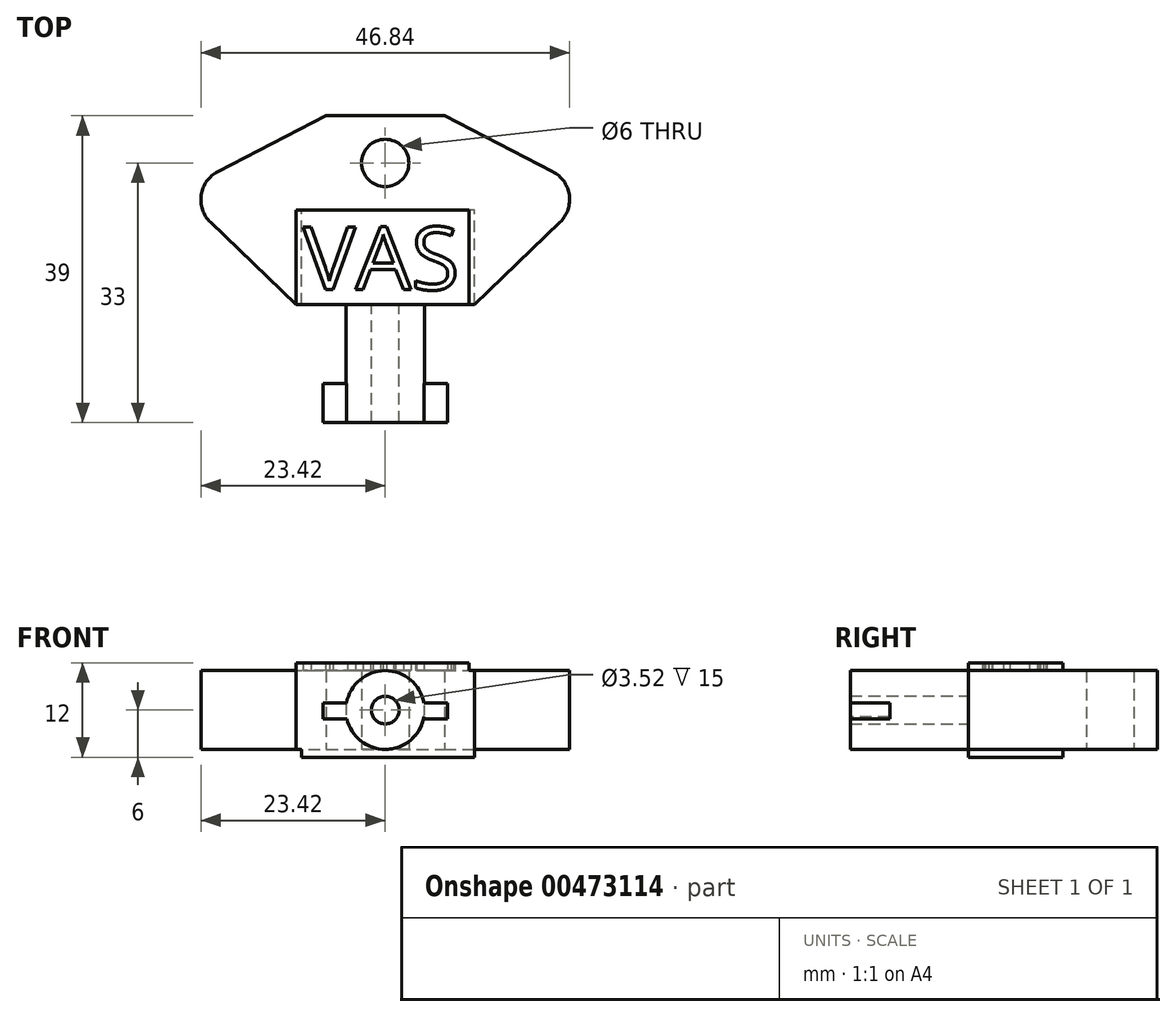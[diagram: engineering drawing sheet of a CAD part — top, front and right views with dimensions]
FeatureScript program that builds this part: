
annotation { "Feature Type Name" : "Feature", "Feature Type Description" : "" }
export const myFeature = defineFeature(function(context is Context, id is Id, definition is map)
    precondition{}
    {
        {
            var Q0;
            Q0=qCreatedBy(makeId("Top.planeOp"),FACE);
            var sketch = newSketch(context, id + "F0", { "sketchPlane" : qUnion([Q0])});
            skCircle(sketch, "E0", {"center": v(0, 0) * mm, "radius": 3 * mm});
            skLineSegment(sketch, "E1", {"start": v(-7.5, 6) * mm, "end": v(7.5, 6) * mm});
            skLineSegment(sketch, "E2", {"start": v(7.5, 6) * mm, "end": v(21.25, -1.1) * mm});
            skLineSegment(sketch, "E3", {"start": v(22.2, -7.53) * mm, "end": v(11.35, -18) * mm});
            skLineSegment(sketch, "E4", {"start": v(-11.35, -18) * mm, "end": v(-22.2, -7.53) * mm});
            skLineSegment(sketch, "E5", {"start": v(-21.25, -1.1) * mm, "end": v(-7.5, 6) * mm});
            skPoint(sketch, "E6", {"position": v(0, -18) * mm});
            skPoint(sketch, "E7", {"position": v(0, 6) * mm});
            skPoint(sketch, "E8.visualSharp", {"position": v(-26.21, -3.66) * mm});
            skArc(sketch, "E8.filletArc", {"start": v(-21.25, -1.1) * mm, "mid": v(-23.38, -4.07) * mm, "end": v(-22.2, -7.53) * mm});
            skPoint(sketch, "E9.visualSharp", {"position": v(26.21, -3.66) * mm});
            skArc(sketch, "E9.filletArc", {"start": v(22.2, -7.53) * mm, "mid": v(23.38, -4.07) * mm, "end": v(21.25, -1.1) * mm});
            skLineSegment(sketch, "E10", {"start": v(11.35, -18) * mm, "end": v(5, -18) * mm});
            skLineSegment(sketch, "E11", {"start": v(-5, -18) * mm, "end": v(-11.35, -18) * mm});
            skLineSegment(sketch, "E12", {"start": v(-5, -18) * mm, "end": v(5, -18) * mm});
            skSolve(sketch);
        }
        {
            var Q0;
            Q0=makeQuery(id+"F0.imprint","IMPRINT",FACE,{"disambiguationData":[TD([[makeQuery(id+"F0.imprint","IMPRINT",EDGE,{"derivedFrom":sQuery(id+"F0.wireOp",EDGE,"E0")}),-1.0]])]});
            extrude(context, id + "F1", {"entities" : qUnion([Q0]), "endBound" : BoundingType.SYMMETRIC, "depth" : 10 * mm});
        }
        {
            var Q0;
            Q0=makeQuery(id+"F1.opExtrude","SWEPT_FACE",FACE,{"disambiguationData":[OSD([sQuery(id+"F0.wireOp",EDGE,"E10"),sQuery(id+"F0.wireOp",EDGE,"E11"),sQuery(id+"F0.wireOp",EDGE,"E12")])]});
            var sketch = newSketch(context, id + "F2", { "sketchPlane" : qUnion([Q0])});
            skCircle(sketch, "E13", {"center": v(0, 0) * mm, "radius": 5 * mm});
            skCircle(sketch, "E14", {"center": v(0, 0) * mm, "radius": 1.76 * mm});
            skSolve(sketch);
        }
        {
            var Q0;
            Q0=makeQuery(id+"F2.imprint","IMPRINT",FACE,{"disambiguationData":[TD([[makeQuery(id+"F2.imprint","IMPRINT",EDGE,{"derivedFrom":sQuery(id+"F2.wireOp",EDGE,"E14")}),-1.0]])]});
            extrude(context, id + "F3", {"entities" : qUnion([Q0]), "operationType" : NewBodyOperationType.ADD, "depth" : 15 * mm});
        }
        {
            var Q0;
            Q0=makeQuery(id+"F3.opExtrude","CAP_FACE",FACE,{"disambiguationData":[OSD([sQuery(id+"F2.wireOp",EDGE,"E13"),sQuery(id+"F2.wireOp",EDGE,"E14")])],"isStart":false});
            var sketch = newSketch(context, id + "F4", { "sketchPlane" : qUnion([Q0])});
            skLineSegment(sketch, "E15.bottom", {"start": v(-4.88, -1.11) * mm, "end": v(-7.88, -1.11) * mm});
            skLineSegment(sketch, "E15.top", {"start": v(-4.88, 0.89) * mm, "end": v(-7.88, 0.89) * mm});
            skLineSegment(sketch, "E15.left", {"start": v(-4.88, -1.11) * mm, "end": v(-4.88, 0.89) * mm});
            skLineSegment(sketch, "E15.right", {"start": v(-7.88, -1.11) * mm, "end": v(-7.88, 0.89) * mm});
            skPoint(sketch, "E16.firstSnap0", {"position": v(-6.38, 0.89) * mm});
            skLineSegment(sketch, "E16.bottom", {"start": v(4.92, 0.89) * mm, "end": v(7.92, 0.89) * mm});
            skLineSegment(sketch, "E16.top", {"start": v(4.92, -1.11) * mm, "end": v(7.92, -1.11) * mm});
            skLineSegment(sketch, "E16.left", {"start": v(4.92, 0.89) * mm, "end": v(4.92, -1.11) * mm});
            skLineSegment(sketch, "E16.right", {"start": v(7.92, 0.89) * mm, "end": v(7.92, -1.11) * mm});
            skSolve(sketch);
        }
        {
            var Q0;
            {var subQ0=sQuery(id+"F4.wireOp",EDGE,"E15.bottom");Q0=makeQuery(id+"F4.imprint","IMPRINT",FACE,{"disambiguationData":[TD([[makeQuery(id+"F4.imprint","IMPRINT",EDGE,{"derivedFrom":subQ0}),-1.0]])]});}
            var Q1;
            {var subQ4=sQuery(id+"F4.wireOp",EDGE,"E16.bottom");Q1=makeQuery(id+"F4.imprint","IMPRINT",FACE,{"disambiguationData":[TD([[makeQuery(id+"F4.imprint","IMPRINT",EDGE,{"derivedFrom":subQ4}),-1.0]])]});}
            extrude(context, id + "F5", {"entities" : qUnion([Q0, Q1]), "operationType" : NewBodyOperationType.ADD, "oppositeDirection" : true, "depth" : 5 * mm});
        }
        {
            var Q0;
            Q0=makeQuery(id+"F1.opExtrude","CAP_FACE",FACE,{"disambiguationData":[OSD([sQuery(id+"F0.wireOp",EDGE,"E0"),sQuery(id+"F0.wireOp",EDGE,"E1"),sQuery(id+"F0.wireOp",EDGE,"E2"),sQuery(id+"F0.wireOp",EDGE,"E3"),sQuery(id+"F0.wireOp",EDGE,"E4"),sQuery(id+"F0.wireOp",EDGE,"E5"),sQuery(id+"F0.wireOp",EDGE,"E8.filletArc"),sQuery(id+"F0.wireOp",EDGE,"E9.filletArc"),sQuery(id+"F0.wireOp",EDGE,"E10"),sQuery(id+"F0.wireOp",EDGE,"E11"),sQuery(id+"F0.wireOp",EDGE,"E12")])],"isStart":true});
            var sketch = newSketch(context, id + "F6", { "sketchPlane" : qUnion([Q0])});
            skLineSegment(sketch, "E17.bottom", {"start": v(11.35, 18) * mm, "end": v(-10.65, 18) * mm});
            skLineSegment(sketch, "E17.top", {"start": v(11.35, 6) * mm, "end": v(-10.65, 6) * mm});
            skLineSegment(sketch, "E17.left", {"start": v(11.35, 18) * mm, "end": v(11.35, 6) * mm});
            skLineSegment(sketch, "E17.right", {"start": v(-10.65, 18) * mm, "end": v(-10.65, 6) * mm});
            skSolve(sketch);
        }
        {
            var Q0;
            Q0 = qSketchRegion(id + "F6", true);
            extrude(context, id + "F7", {"entities" : qUnion([Q0]), "operationType" : NewBodyOperationType.ADD, "depth" : 1 * mm});
        }
        {
            var Q0;
            Q0=makeQuery(id+"F1.opExtrude","CAP_FACE",FACE,{"disambiguationData":[OSD([sQuery(id+"F0.wireOp",EDGE,"E0"),sQuery(id+"F0.wireOp",EDGE,"E1"),sQuery(id+"F0.wireOp",EDGE,"E2"),sQuery(id+"F0.wireOp",EDGE,"E3"),sQuery(id+"F0.wireOp",EDGE,"E4"),sQuery(id+"F0.wireOp",EDGE,"E5"),sQuery(id+"F0.wireOp",EDGE,"E8.filletArc"),sQuery(id+"F0.wireOp",EDGE,"E9.filletArc"),sQuery(id+"F0.wireOp",EDGE,"E10"),sQuery(id+"F0.wireOp",EDGE,"E11"),sQuery(id+"F0.wireOp",EDGE,"E12")])],"isStart":false});
            var sketch = newSketch(context, id + "F8", { "sketchPlane" : qUnion([Q0])});
            skLineSegment(sketch, "E18.bottom", {"start": v(-11.35, -18) * mm, "end": v(10.65, -18) * mm});
            skLineSegment(sketch, "E18.top", {"start": v(-11.35, -6) * mm, "end": v(10.65, -6) * mm});
            skLineSegment(sketch, "E18.left", {"start": v(-11.35, -18) * mm, "end": v(-11.35, -6) * mm});
            skLineSegment(sketch, "E18.right", {"start": v(10.65, -18) * mm, "end": v(10.65, -6) * mm});
            skText(sketch, "E19", { "text": "VAS", "fontName": "OpenSans-Regular.ttf"});
            const initialGuessF8  = {"E19": [-0.01041, -0.0161, 1, 0, 0.00803]};
            skSetInitialGuess(sketch, initialGuessF8);
            skSolve(sketch);
        }
        {
            var Q0;
            Q0=makeQuery(id+"F8.imprint","IMPRINT",FACE,{"disambiguationData":[TD([[makeQuery(id+"F8.imprint","IMPRINT",EDGE,{"derivedFrom":sQuery(id+"F8.wireOp",EDGE,"E18.top")}),-1.0]])]});
            extrude(context, id + "F9", {"entities" : qUnion([Q0]), "operationType" : NewBodyOperationType.ADD, "depth" : 1 * mm});
        }
        {
            var Q0;
            Q0=makeQuery(id+"F8.imprint","IMPRINT",FACE,{"disambiguationData":[TD([[makeQuery(id+"F8.imprint","IMPRINT",EDGE,{"derivedFrom":sQuery(id+"F8.wireOp",EDGE,"E19.sketch_text.stroke-17")}),1.0]])]});
            extrude(context, id + "F10", {"entities" : qUnion([Q0]), "operationType" : NewBodyOperationType.ADD, "depth" : 1 * mm});
        }
    });
